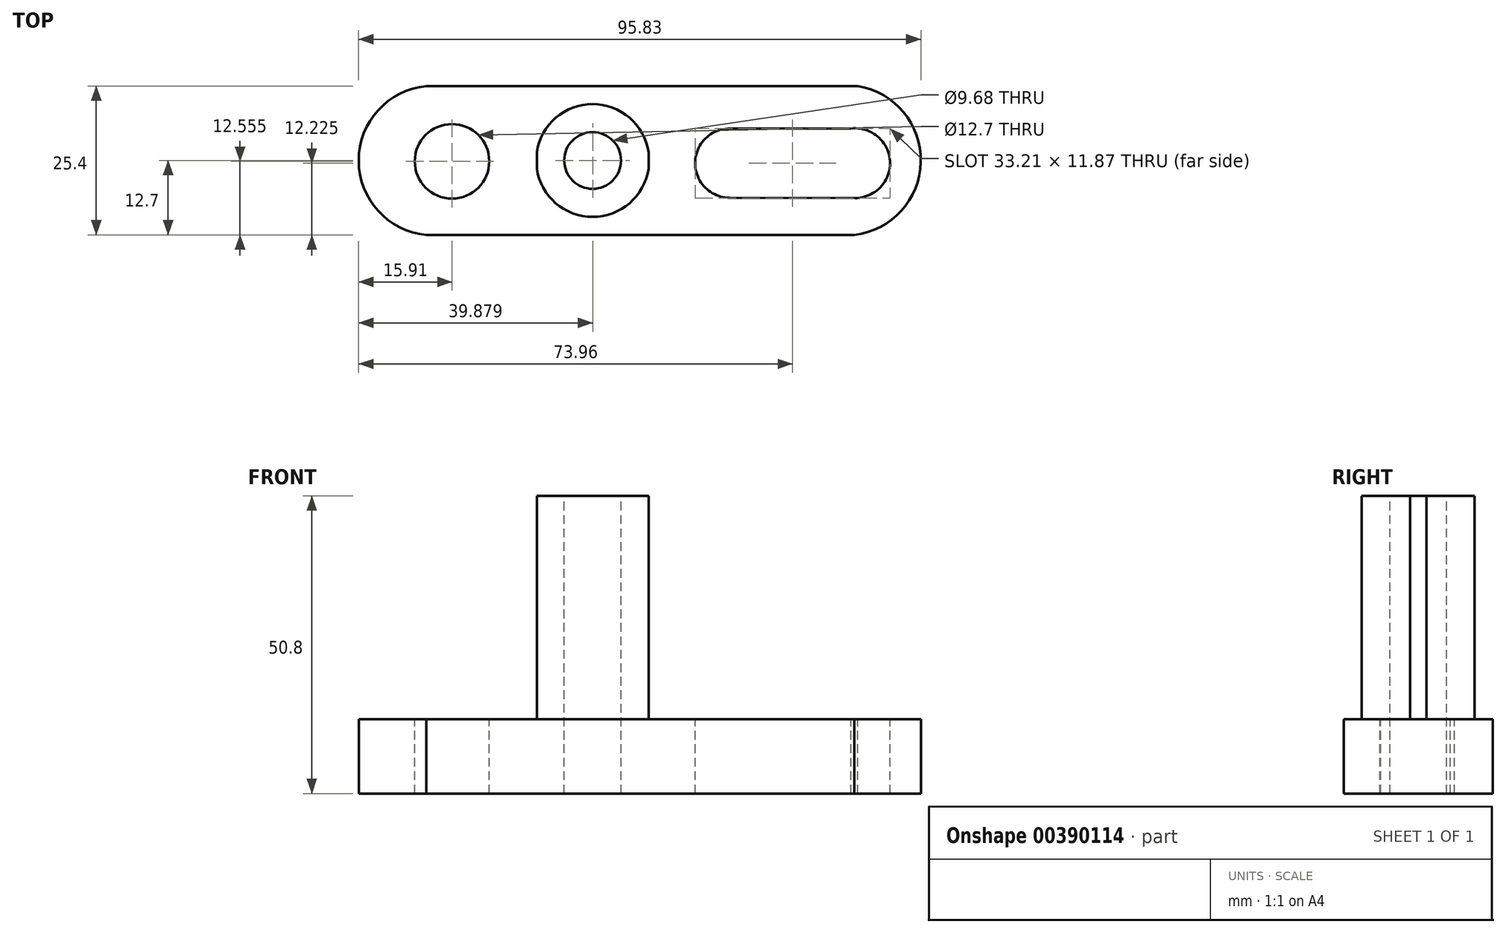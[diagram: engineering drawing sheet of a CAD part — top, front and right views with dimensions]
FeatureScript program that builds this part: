
annotation { "Feature Type Name" : "Feature", "Feature Type Description" : "" }
export const myFeature = defineFeature(function(context is Context, id is Id, definition is map)
    precondition{}
    {
        {
            var Q0;
            Q0=qCreatedBy(makeId("Front.planeOp"),FACE);
            var sketch = newSketch(context, id + "F0", { "sketchPlane" : qUnion([Q0])});
            skLineSegment(sketch, "E0", {"start": v(0, 0) * mm, "end": v(-101.6, 0) * mm});
            skLineSegment(sketch, "E1", {"start": v(-101.6, 0) * mm, "end": v(-101.6, 12.7) * mm});
            skLineSegment(sketch, "E2", {"start": v(-101.6, 12.7) * mm, "end": v(-68.83, 12.7) * mm});
            skLineSegment(sketch, "E3", {"start": v(-68.83, 12.7) * mm, "end": v(-68.83, 50.8) * mm});
            skLineSegment(sketch, "E4", {"start": v(-68.83, 50.8) * mm, "end": v(-49.78, 50.8) * mm});
            skLineSegment(sketch, "E5", {"start": v(-49.78, 50.8) * mm, "end": v(-49.78, 12.7) * mm});
            skLineSegment(sketch, "E6", {"start": v(-49.78, 12.7) * mm, "end": v(0, 12.7) * mm});
            skLineSegment(sketch, "E7", {"start": v(0, 12.7) * mm, "end": v(0, 0) * mm});
            skSolve(sketch);
        }
        {
            var Q0;
            Q0 = qSketchRegion(id + "F0", true);
            extrude(context, id + "F1", {"entities" : qUnion([Q0]), "depth" : 25.4 * mm});
        }
        {
            var Q0;
            Q0=makeQuery(id+"F1.opExtrude","SWEPT_FACE",FACE,{"disambiguationData":[OSD([sQuery(id+"F0.wireOp",EDGE,"E4")])]});
            var sketch = newSketch(context, id + "F2", { "sketchPlane" : qUnion([Q0])});
            skCircle(sketch, "E8", {"center": v(-59.3, -12.7) * mm, "radius": 4.84 * mm});
            skPoint(sketch, "E8.centerSnap0", {"position": v(-49.78, -12.7) * mm});
            skPoint(sketch, "E8.centerSnap1", {"position": v(-59.3, 0) * mm});
            skSolve(sketch);
        }
        {
            var Q0;
            Q0 = qSketchRegion(id + "F2", true);
            extrude(context, id + "F3", {"entities" : qUnion([Q0]), "operationType" : NewBodyOperationType.REMOVE, "oppositeDirection" : true, "depth" : 50.8 * mm});
        }
        {
            var Q0;
            Q0=makeQuery(id+"F1.opExtrude","SWEPT_FACE",FACE,{"disambiguationData":[OSD([sQuery(id+"F0.wireOp",EDGE,"E6")])]});
            var sketch = newSketch(context, id + "F4", { "sketchPlane" : qUnion([Q0])});
            skCircle(sketch, "E9", {"center": v(-35.91, -13.15) * mm, "radius": 5.91 * mm});
            skCircle(sketch, "E10", {"center": v(-14.56, -13.15) * mm, "radius": 5.95 * mm});
            skLineSegment(sketch, "E11", {"start": v(-13.85, -7.24) * mm, "end": v(-35.91, -7.24) * mm});
            skLineSegment(sketch, "E12", {"start": v(-35.91, -19.07) * mm, "end": v(-14.57, -19.1) * mm});
            skArc(sketch, "E13", {"start": v(-17.65, -25.4) * mm, "mid": v(-3.36, -12.34) * mm, "end": v(-18.27, 0) * mm});
            skSolve(sketch);
        }
        {
            var Q0;
            {var subQ0=sQuery(id+"F4.wireOp",EDGE,"E11");var subQ1=sQuery(id+"F4.wireOp",EDGE,"E10");var subQ2=makeQuery(id+"F4.imprint","INTERSECT",VERTEX,{"disambiguationData":[OD(0.0)],"derivedFrom":[subQ1,subQ0]});Q0=makeQuery(id+"F4.imprint","IMPRINT",FACE,{"disambiguationData":[TD([[makeQuery(id+"F4.imprint","IMPRINT",EDGE,{"disambiguationData":[TD([[subQ2,-1.0]])],"derivedFrom":subQ1}),1.0]])]});}
            var Q1;
            {var subQ0=sQuery(id+"F4.wireOp",EDGE,"t4yfd8No-aidi-XixL-hFha-ibOwOurlKBVg");Q1=makeQuery(id+"F4.imprint","IMPRINT",FACE,{"disambiguationData":[TD([[makeQuery(id+"F4.imprint","IMPRINT",EDGE,{"derivedFrom":subQ0}),-1.0]])]});}
            var Q2;
            {var subQ0=sQuery(id+"F4.wireOp",EDGE,"E10");var subQ1=makeQuery(id+"F4.imprint","INTERSECT",VERTEX,{"derivedFrom":[subQ0,sQuery(id+"F4.wireOp",EDGE,"E12")]});Q2=makeQuery(id+"F4.imprint","IMPRINT",FACE,{"disambiguationData":[TD([[makeQuery(id+"F4.imprint","IMPRINT",EDGE,{"disambiguationData":[TD([[subQ1,1.0]])],"derivedFrom":subQ0}),1.0]])]});}
            var Q3;
            {var subQ1=sQuery(id+"F0.wireOp",EDGE,"E6");var subQ6=makeQuery(id+"F1.opExtrude","SWEPT_EDGE",EDGE,{"disambiguationData":[OSD([subQ1,sQuery(id+"F0.wireOp",EDGE,"E7")])]});Q3=makeQuery(id+"F4.imprint","IMPRINT",FACE,{"disambiguationData":[TD([[makeQuery(id+"F4.imprint","IMPRINT",EDGE,{"derivedFrom":subQ6}),1.0]])]});}
            var Q4;
            {var subQ3=sQuery(id+"F4.wireOp",EDGE,"E12");Q4=makeQuery(id+"F4.imprint","IMPRINT",FACE,{"disambiguationData":[TD([[makeQuery(id+"F4.imprint","IMPRINT",EDGE,{"derivedFrom":subQ3}),1.0]])]});}
            var Q5;
            {var subQ0=sQuery(id+"F4.wireOp",EDGE,"E9");var subQ2=makeQuery(id+"F4.imprint","IMPRINT",VERTEX,{"derivedFrom":subQ0});Q5=makeQuery(id+"F4.imprint","IMPRINT",FACE,{"disambiguationData":[TD([[makeQuery(id+"F4.imprint","IMPRINT",EDGE,{"disambiguationData":[TD([[subQ2,1.0]])],"derivedFrom":subQ0}),1.0]])]});}
            extrude(context, id + "F5", {"entities" : qUnion([Q0, Q1, Q2, Q3, Q4, Q5]), "operationType" : NewBodyOperationType.REMOVE, "oppositeDirection" : true, "depth" : 25.4 * mm});
        }
        {
            var Q0;
            Q0 = qSketchRegion(id + "F4", true);
            extrude(context, id + "F6", {"entities" : qUnion([Q0]), "operationType" : NewBodyOperationType.REMOVE, "oppositeDirection" : true, "depth" : 25.4 * mm});
        }
        {
            var Q0;
            Q0=makeQuery(id+"F1.opExtrude","SWEPT_FACE",FACE,{"disambiguationData":[OSD([sQuery(id+"F0.wireOp",EDGE,"E2")])]});
            var sketch = newSketch(context, id + "F7", { "sketchPlane" : qUnion([Q0])});
            skCircle(sketch, "E14", {"center": v(-83.27, -12.84) * mm, "radius": 6.35 * mm});
            skArc(sketch, "E15", {"start": v(-85.21, 0) * mm, "mid": v(-99.18, -12.7) * mm, "end": v(-85.21, -25.4) * mm});
            skSolve(sketch);
        }
        {
            var Q0;
            {var subQ0=sQuery(id+"F7.wireOp",EDGE,"xAbWXPtO-HVy7-gJ9G-RNCH-uKj4zDXlxugy");Q0=makeQuery(id+"F7.imprint","IMPRINT",FACE,{"disambiguationData":[TD([[makeQuery(id+"F7.imprint","IMPRINT",EDGE,{"derivedFrom":subQ0}),-1.0]])]});}
            var Q1;
            Q1=makeQuery(id+"F7.imprint","IMPRINT",FACE,{"disambiguationData":[TD([[makeQuery(id+"F7.imprint","IMPRINT",EDGE,{"derivedFrom":sQuery(id+"F7.wireOp",EDGE,"E14")}),1.0]])]});
            var Q2;
            {var subQ1=sQuery(id+"F0.wireOp",EDGE,"E2");var subQ6=makeQuery(id+"F1.opExtrude","SWEPT_EDGE",EDGE,{"disambiguationData":[OSD([sQuery(id+"F0.wireOp",EDGE,"E1"),subQ1])]});Q2=makeQuery(id+"F7.imprint","IMPRINT",FACE,{"disambiguationData":[TD([[makeQuery(id+"F7.imprint","IMPRINT",EDGE,{"derivedFrom":subQ6}),-1.0]])]});}
            extrude(context, id + "F8", {"entities" : qUnion([Q0, Q1, Q2]), "operationType" : NewBodyOperationType.REMOVE, "oppositeDirection" : true, "depth" : 25.4 * mm});
        }
        {
            var Q0;
            Q0=makeQuery(id+"F1.opExtrude","SWEPT_FACE",FACE,{"disambiguationData":[OSD([sQuery(id+"F0.wireOp",EDGE,"E4")])]});
            var sketch = newSketch(context, id + "F9", { "sketchPlane" : qUnion([Q0])});
            skCircle(sketch, "E16", {"center": v(-59.3, -12.7) * mm, "radius": 9.63 * mm});
            skSolve(sketch);
        }
        {
            var Q0;
            {var subQ0=sQuery(id+"F9.wireOp",EDGE,"RVtgrbNs-BNg2-VQdT-eFMK-Vb1J679BN78J");Q0=makeQuery(id+"F9.imprint","IMPRINT",FACE,{"disambiguationData":[TD([[makeQuery(id+"F9.imprint","IMPRINT",EDGE,{"derivedFrom":subQ0}),-1.0]])]});}
            var Q1;
            {var subQ1=sQuery(id+"F0.wireOp",EDGE,"E4");var subQ6=makeQuery(id+"F1.opExtrude","CAP_EDGE",EDGE,{"disambiguationData":[OSD([subQ1])],"isStart":true});Q1=makeQuery(id+"F9.imprint","IMPRINT",FACE,{"disambiguationData":[TD([[makeQuery(id+"F9.imprint","IMPRINT",EDGE,{"derivedFrom":subQ6}),-1.0]])]});}
            var Q2;
            {var subQ1=sQuery(id+"F0.wireOp",EDGE,"E4");var subQ6=makeQuery(id+"F1.opExtrude","CAP_EDGE",EDGE,{"disambiguationData":[OSD([subQ1])],"isStart":false});Q2=makeQuery(id+"F9.imprint","IMPRINT",FACE,{"disambiguationData":[TD([[makeQuery(id+"F9.imprint","IMPRINT",EDGE,{"derivedFrom":subQ6}),1.0]])]});}
            extrude(context, id + "F10", {"entities" : qUnion([Q0, Q1, Q2]), "operationType" : NewBodyOperationType.REMOVE, "oppositeDirection" : true, "depth" : 38.1 * mm});
        }
        {
            var Q0;
            Q0 = qSketchRegion(id + "F7", true);
            extrude(context, id + "F11", {"entities" : qUnion([Q0]), "depth" : 25.4 * mm});
        }
        {
            var Q0;
            Q0=makeQuery(id+"F11.opExtrude","CAP_FACE",FACE,{"disambiguationData":[OSD([sQuery(id+"F7.wireOp",EDGE,"E14")])],"isStart":false});
            extrude(context, id + "F12", {"entities" : qUnion([Q0]), "operationType" : NewBodyOperationType.REMOVE, "oppositeDirection" : true, "depth" : 25.4 * mm});
        }
    });
